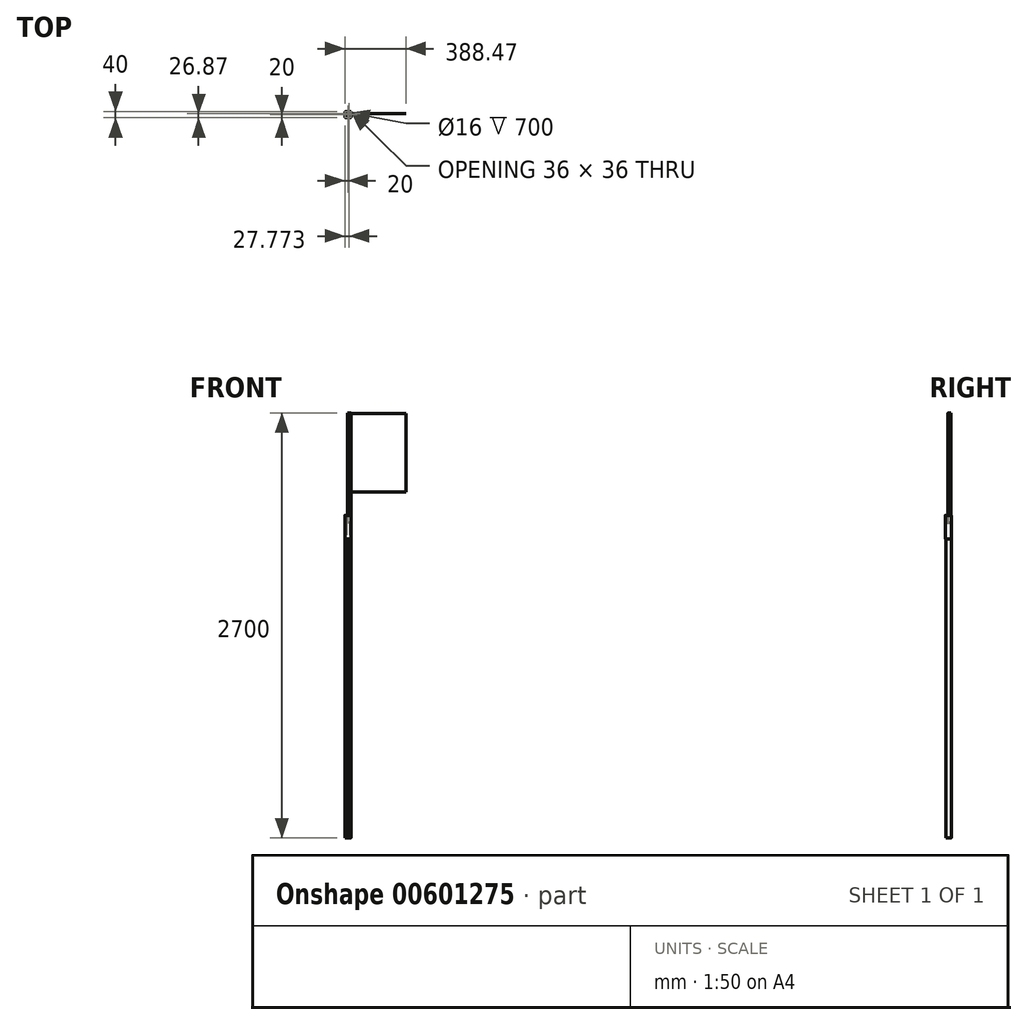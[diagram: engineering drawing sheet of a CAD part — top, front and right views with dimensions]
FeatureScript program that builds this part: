
annotation { "Feature Type Name" : "Feature", "Feature Type Description" : "" }
export const myFeature = defineFeature(function(context is Context, id is Id, definition is map)
    precondition{}
    {
        {
            var Q0;
            Q0=qCreatedBy(makeId("Top.planeOp"),FACE);
            var sketch = newSketch(context, id + "F0", { "sketchPlane" : qUnion([Q0])});
            skLineSegment(sketch, "E0.bottom", {"start": v(12.5, -17.5) * mm, "end": v(-12.5, -17.5) * mm});
            skLineSegment(sketch, "E0.top", {"start": v(12.5, 17.5) * mm, "end": v(-12.5, 17.5) * mm});
            skLineSegment(sketch, "E0.left", {"start": v(17.5, -12.5) * mm, "end": v(17.5, 12.5) * mm});
            skLineSegment(sketch, "E0.right", {"start": v(-17.5, -12.5) * mm, "end": v(-17.5, 12.5) * mm});
            skPoint(sketch, "E0.middle", {"position": v(0, 0) * mm});
            skPoint(sketch, "E1.visualSharp", {"position": v(-17.5, 17.5) * mm});
            skArc(sketch, "E1.filletArc", {"start": v(-12.5, 17.5) * mm, "mid": v(-16.04, 16.04) * mm, "end": v(-17.5, 12.5) * mm});
            skPoint(sketch, "E2.visualSharp", {"position": v(17.5, 17.5) * mm});
            skArc(sketch, "E2.filletArc", {"start": v(17.5, 12.5) * mm, "mid": v(16.04, 16.04) * mm, "end": v(12.5, 17.5) * mm});
            skPoint(sketch, "E3.visualSharp", {"position": v(17.5, -17.5) * mm});
            skArc(sketch, "E3.filletArc", {"start": v(12.5, -17.5) * mm, "mid": v(16.04, -16.04) * mm, "end": v(17.5, -12.5) * mm});
            skPoint(sketch, "E4.visualSharp", {"position": v(-17.5, -17.5) * mm});
            skArc(sketch, "E4.filletArc", {"start": v(-17.5, -12.5) * mm, "mid": v(-16.04, -16.04) * mm, "end": v(-12.5, -17.5) * mm});
            skLineSegment(sketch, "E5.0", {"start": v(-15.5, -12.5) * mm, "end": v(-15.5, 12.5) * mm});
            skLineSegment(sketch, "E5.1", {"start": v(12.5, -15.5) * mm, "end": v(-12.5, -15.5) * mm});
            skLineSegment(sketch, "E5.2", {"start": v(15.5, -12.5) * mm, "end": v(15.5, 12.5) * mm});
            skLineSegment(sketch, "E5.3", {"start": v(12.5, 15.5) * mm, "end": v(-12.5, 15.5) * mm});
            skPoint(sketch, "E6.visualSharp", {"position": v(-15.5, 15.5) * mm});
            skArc(sketch, "E6.filletArc", {"start": v(-12.5, 15.5) * mm, "mid": v(-14.62, 14.62) * mm, "end": v(-15.5, 12.5) * mm});
            skPoint(sketch, "E7.visualSharp", {"position": v(15.5, 15.5) * mm});
            skArc(sketch, "E7.filletArc", {"start": v(15.5, 12.5) * mm, "mid": v(14.62, 14.62) * mm, "end": v(12.5, 15.5) * mm});
            skPoint(sketch, "E8.visualSharp", {"position": v(15.5, -15.5) * mm});
            skArc(sketch, "E8.filletArc", {"start": v(12.5, -15.5) * mm, "mid": v(14.62, -14.62) * mm, "end": v(15.5, -12.5) * mm});
            skPoint(sketch, "E9.visualSharp", {"position": v(-15.5, -15.5) * mm});
            skArc(sketch, "E9.filletArc", {"start": v(-15.5, -12.5) * mm, "mid": v(-14.62, -14.62) * mm, "end": v(-12.5, -15.5) * mm});
            skSolve(sketch);
        }
        {
            var Q0;
            Q0 = qSketchRegion(id + "F0", true);
            extrude(context, id + "F1", {"entities" : qUnion([Q0]), "oppositeDirection" : true, "depth" : 2000 * mm, "offsetDistance" : 25 * mm});
        }
        {
            var Q0;
            Q0=qCreatedBy(makeId("Top.planeOp"),FACE);
            var sketch = newSketch(context, id + "F2", { "sketchPlane" : qUnion([Q0])});
            skLineSegment(sketch, "E10.bottom", {"start": v(10, -23.26) * mm, "end": v(-10, -23.26) * mm});
            skLineSegment(sketch, "E10.top", {"start": v(10, -11.16) * mm, "end": v(-10, -11.16) * mm});
            skLineSegment(sketch, "E10.left", {"start": v(10, -23.26) * mm, "end": v(10, -11.16) * mm});
            skLineSegment(sketch, "E10.right", {"start": v(-10, -23.26) * mm, "end": v(-10, -11.16) * mm});
            skPoint(sketch, "E10.middle", {"position": v(0, -17.21) * mm});
            skSolve(sketch);
        }
        {
            var Q0;
            Q0 = qSketchRegion(id + "F2", true);
            extrude(context, id + "F3", {"entities" : qUnion([Q0]), "operationType" : NewBodyOperationType.REMOVE, "endBound" : BoundingType.THROUGH_ALL, "oppositeDirection" : true, "depth" : 25 * mm, "offsetDistance" : 25 * mm});
        }
        {
            var Q0;
            Q0=qCreatedBy(makeId("Top.planeOp"),FACE);
            var sketch = newSketch(context, id + "F4", { "sketchPlane" : qUnion([Q0])});
            skLineSegment(sketch, "E11.bottom", {"start": v(-15, -20) * mm, "end": v(15, -20) * mm});
            skLineSegment(sketch, "E11.top", {"start": v(-15, 20) * mm, "end": v(15, 20) * mm});
            skLineSegment(sketch, "E11.left", {"start": v(-20, -15) * mm, "end": v(-20, 15) * mm});
            skLineSegment(sketch, "E11.right", {"start": v(20, -15) * mm, "end": v(20, 15) * mm});
            skPoint(sketch, "E11.middle", {"position": v(0, 0) * mm});
            skPoint(sketch, "E12.visualSharp", {"position": v(-20, 20) * mm});
            skArc(sketch, "E12.filletArc", {"start": v(-15, 20) * mm, "mid": v(-18.54, 18.54) * mm, "end": v(-20, 15) * mm});
            skPoint(sketch, "E13.visualSharp", {"position": v(20, 20) * mm});
            skArc(sketch, "E13.filletArc", {"start": v(20, 15) * mm, "mid": v(18.54, 18.54) * mm, "end": v(15, 20) * mm});
            skPoint(sketch, "E14.visualSharp", {"position": v(20, -20) * mm});
            skArc(sketch, "E14.filletArc", {"start": v(15, -20) * mm, "mid": v(18.54, -18.54) * mm, "end": v(20, -15) * mm});
            skPoint(sketch, "E15.visualSharp", {"position": v(-20, -20) * mm});
            skArc(sketch, "E15.filletArc", {"start": v(-20, -15) * mm, "mid": v(-18.54, -18.54) * mm, "end": v(-15, -20) * mm});
            skLineSegment(sketch, "E16.0", {"start": v(-15, 18) * mm, "end": v(15, 18) * mm});
            skArc(sketch, "E16.1", {"start": v(18, 15) * mm, "mid": v(17.12, 17.12) * mm, "end": v(15, 18) * mm});
            skArc(sketch, "E16.2", {"start": v(-15, 18) * mm, "mid": v(-17.12, 17.12) * mm, "end": v(-18, 15) * mm});
            skLineSegment(sketch, "E16.3", {"start": v(18, -15) * mm, "end": v(18, 15) * mm});
            skLineSegment(sketch, "E16.4", {"start": v(-18, -15) * mm, "end": v(-18, 15) * mm});
            skArc(sketch, "E16.5", {"start": v(-18, -15) * mm, "mid": v(-17.12, -17.12) * mm, "end": v(-15, -18) * mm});
            skLineSegment(sketch, "E16.6", {"start": v(-15, -18) * mm, "end": v(15, -18) * mm});
            skArc(sketch, "E16.7", {"start": v(15, -18) * mm, "mid": v(17.12, -17.12) * mm, "end": v(18, -15) * mm});
            skSolve(sketch);
        }
        {
            var Q0;
            Q0 = qSketchRegion(id + "F4", true);
            extrude(context, id + "F5", {"entities" : qUnion([Q0]), "oppositeDirection" : true, "depth" : 100 * mm, "offsetDistance" : 25 * mm, "hasSecondDirection" : true, "secondDirectionOppositeDirection" : false, "secondDirectionDepth" : 50 * mm});
        }
        {
            var Q0;
            Q0=qCreatedBy(makeId("Top.planeOp"),FACE);
            var sketch = newSketch(context, id + "F6", { "sketchPlane" : qUnion([Q0])});
            skCircle(sketch, "E17", {"center": v(7.77, 6.87) * mm, "radius": 10 * mm});
            skPoint(sketch, "E17.first.point", {"position": v(7.06, 16.84) * mm});
            skPoint(sketch, "E17.second.point", {"position": v(8.29, -3.12) * mm});
            skPoint(sketch, "E17.third.point", {"position": v(-2.04, 4.94) * mm});
            skCircle(sketch, "E18.0", {"center": v(7.77, 6.87) * mm, "radius": 8 * mm});
            skSolve(sketch);
        }
        {
            var Q0;
            Q0 = qSketchRegion(id + "F6", true);
            extrude(context, id + "F7", {"entities" : qUnion([Q0]), "depth" : 700 * mm, "offsetDistance" : 25 * mm});
        }
        {
            var Q0;
            Q0=qCreatedBy(makeId("Front.planeOp"),FACE);
            cPlane(context, id + "F8", {"entities" : qUnion([Q0]), "cplaneType" : CPlaneType.OFFSET, "offset" : 7 * mm, "oppositeDirection" : true, "width" : 150 * mm, "height" : 150 * mm});
        }
        {
            var Q0;
            Q0=qCreatedBy(id+"F8.planeOp",FACE);
            var sketch = newSketch(context, id + "F9", { "sketchPlane" : qUnion([Q0])});
            skLineSegment(sketch, "E19.bottom", {"start": v(18.47, 697.58) * mm, "end": v(368.47, 697.58) * mm});
            skLineSegment(sketch, "E19.top", {"start": v(18.47, 197.58) * mm, "end": v(368.47, 197.58) * mm});
            skLineSegment(sketch, "E19.left", {"start": v(18.47, 697.58) * mm, "end": v(18.47, 197.58) * mm});
            skLineSegment(sketch, "E19.right", {"start": v(368.47, 697.58) * mm, "end": v(368.47, 197.58) * mm});
            skSolve(sketch);
        }
        {
            var Q0;
            Q0 = qSketchRegion(id + "F9", true);
            extrude(context, id + "F10", {"entities" : qUnion([Q0]), "depth" : 1 * mm, "offsetDistance" : 25 * mm});
        }
    });
